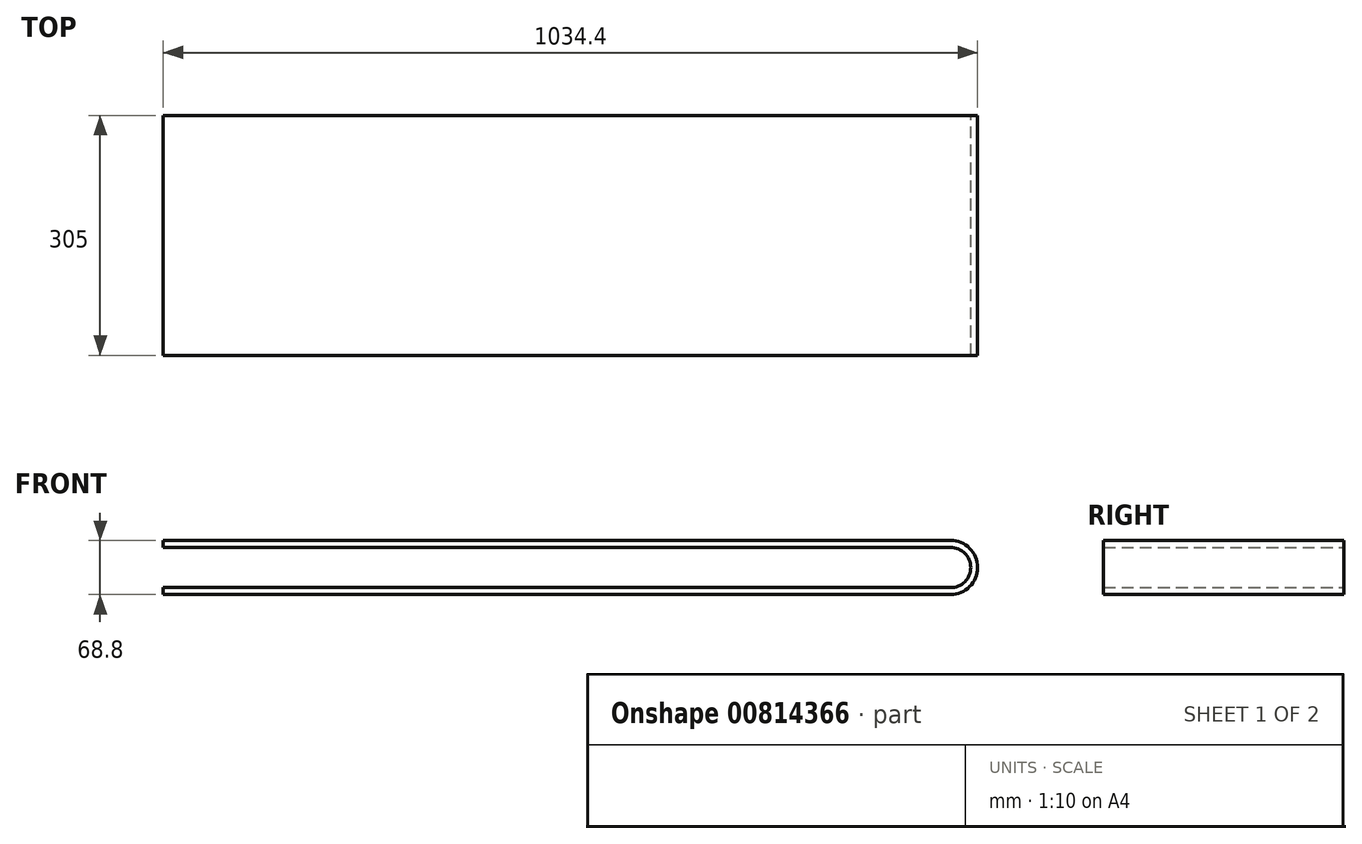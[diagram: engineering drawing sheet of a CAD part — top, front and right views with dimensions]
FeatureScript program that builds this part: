
annotation { "Feature Type Name" : "Feature", "Feature Type Description" : "" }
export const myFeature = defineFeature(function(context is Context, id is Id, definition is map)
    precondition{}
    {
        {
            var Q0;
            Q0=qCreatedBy(makeId("Front.planeOp"),FACE);
            var sketch = newSketch(context, id + "F0", { "sketchPlane" : qUnion([Q0])});
            skLineSegment(sketch, "E0", {"start": v(-31.8, 73.86) * mm, "end": v(468.2, 73.86) * mm});
            skLineSegment(sketch, "E1", {"start": v(468.2, 73.86) * mm, "end": v(468.2, 82.66) * mm});
            skLineSegment(sketch, "E2", {"start": v(-31.8, 82.66) * mm, "end": v(468.2, 82.66) * mm});
            skLineSegment(sketch, "E3", {"start": v(-31.8, 22.66) * mm, "end": v(101.86, 22.66) * mm});
            skArc(sketch, "E4.MirrorCS", {"start": v(968.2, 73.86) * mm, "mid": v(993.8, 48.26) * mm, "end": v(968.2, 22.66) * mm});
            skLineSegment(sketch, "E5.MirrorCS", {"start": v(968.2, 73.86) * mm, "end": v(468.2, 73.86) * mm});
            skArc(sketch, "E6.MirrorCS", {"start": v(968.2, 82.66) * mm, "mid": v(1002.6, 48.26) * mm, "end": v(968.2, 13.86) * mm});
            skLineSegment(sketch, "E7.MirrorCS", {"start": v(968.2, 22.66) * mm, "end": v(834.55, 22.66) * mm});
            skLineSegment(sketch, "E8.MirrorCS", {"start": v(968.2, 82.66) * mm, "end": v(468.2, 82.66) * mm});
            skLineSegment(sketch, "E9", {"start": v(101.86, 22.66) * mm, "end": v(834.55, 22.66) * mm});
            skLineSegment(sketch, "E10", {"start": v(-31.8, 13.86) * mm, "end": v(968.2, 13.86) * mm});
            skLineSegment(sketch, "E11", {"start": v(468.2, 13.86) * mm, "end": v(468.2, -142.37) * mm});
            skLineSegment(sketch, "E12", {"start": v(-31.8, 73.86) * mm, "end": v(-31.8, 82.66) * mm});
            skLineSegment(sketch, "E13", {"start": v(-31.8, 13.86) * mm, "end": v(-31.8, 22.66) * mm});
            skSolve(sketch);
        }
        {
            var Q0;
            Q0 = qSketchRegion(id + "F0", true);
            extrude(context, id + "F1", {"entities" : qUnion([Q0]), "depth" : 305 * mm, "offsetDistance" : 25 * mm});
        }
    });
